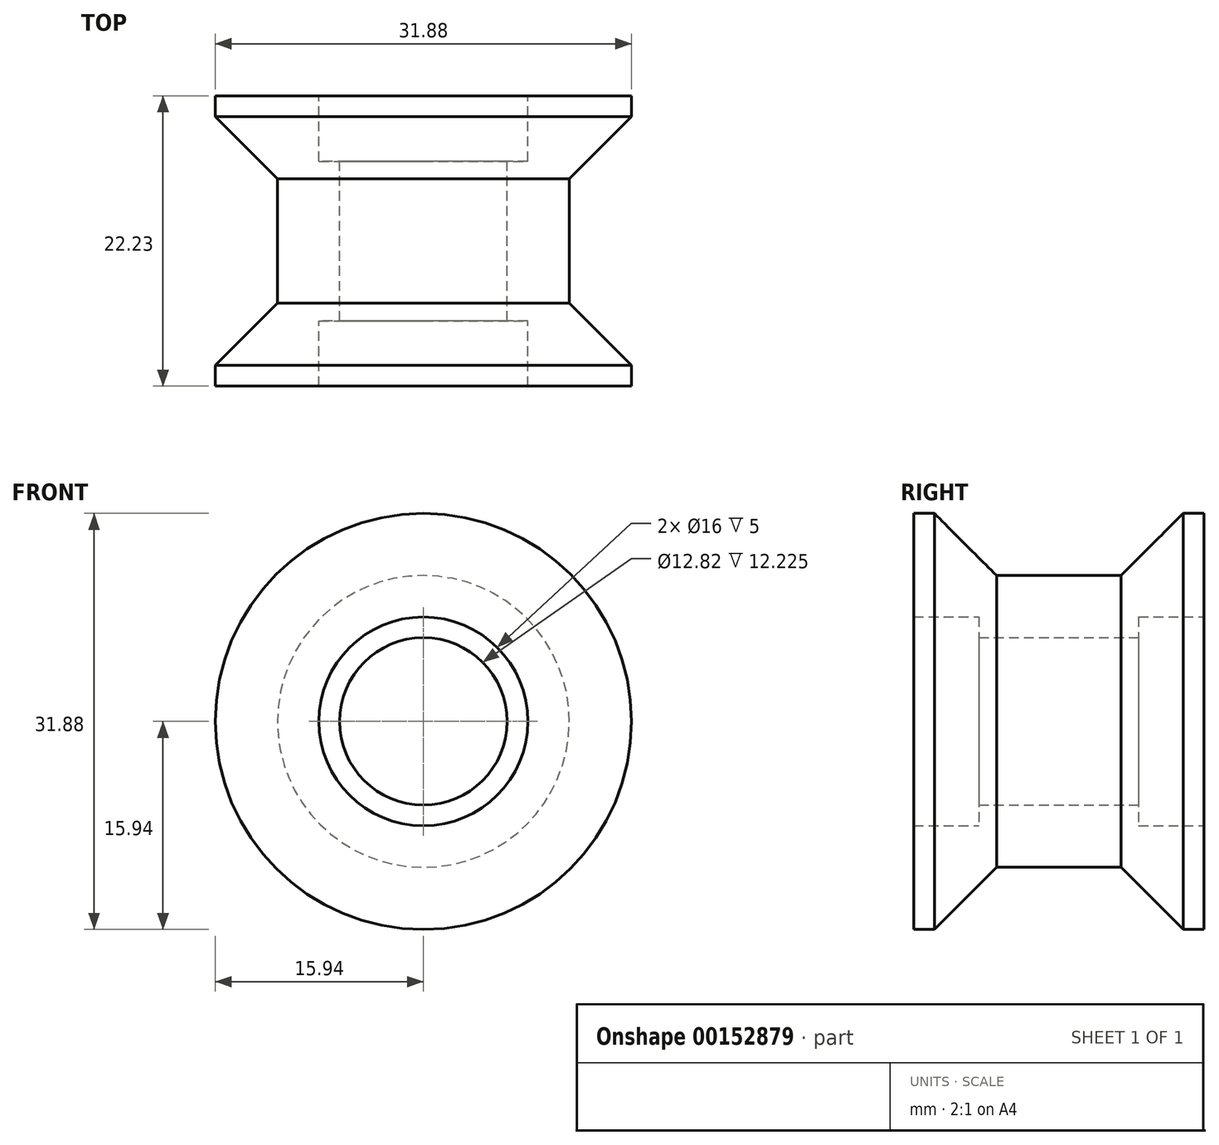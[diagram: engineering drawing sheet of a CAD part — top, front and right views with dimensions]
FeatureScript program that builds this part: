
annotation { "Feature Type Name" : "Feature", "Feature Type Description" : "" }
export const myFeature = defineFeature(function(context is Context, id is Id, definition is map)
    precondition{}
    {
        {
            var Q0;
            Q0=qCreatedBy(makeId("Top.planeOp"),FACE);
            var sketch = newSketch(context, id + "F0", { "sketchPlane" : qUnion([Q0])});
            skLineSegment(sketch, "E0", {"start": v(-15.94, 0) * mm, "end": v(-15.94, 1.59) * mm});
            skLineSegment(sketch, "E1", {"start": v(-15.94, 1.59) * mm, "end": v(-11.18, 6.35) * mm});
            skLineSegment(sketch, "E2", {"start": v(-11.18, 6.35) * mm, "end": v(-11.18, 15.88) * mm});
            skLineSegment(sketch, "E3", {"start": v(-11.18, 15.88) * mm, "end": v(-15.94, 20.64) * mm});
            skLineSegment(sketch, "E4", {"start": v(-15.94, 20.64) * mm, "end": v(-15.94, 22.23) * mm});
            skLineSegment(sketch, "E5", {"start": v(-15.94, 22.23) * mm, "end": v(-8, 22.23) * mm});
            skLineSegment(sketch, "E6.bottom", {"start": v(0, 0) * mm, "end": v(-8, 0) * mm, "construction": true});
            skLineSegment(sketch, "E6.top", {"start": v(0, 22.23) * mm, "end": v(-8, 22.23) * mm, "construction": true});
            skLineSegment(sketch, "E6.left", {"start": v(0, 0) * mm, "end": v(0, 22.23) * mm, "construction": true});
            skLineSegment(sketch, "E7", {"start": v(-8, 0) * mm, "end": v(-15.94, 0) * mm});
            skLineSegment(sketch, "E8", {"start": v(-15.94, 1.59) * mm, "end": v(-15.94, 20.64) * mm, "construction": true});
            skLineSegment(sketch, "E9", {"start": v(-15.94, 11.11) * mm, "end": v(-11.18, 11.11) * mm, "construction": true});
            skLineSegment(sketch, "E10", {"start": v(-11.18, 11.11) * mm, "end": v(-8, 11.11) * mm, "construction": true});
            skLineSegment(sketch, "E11.bottom", {"start": v(-8, 17.23) * mm, "end": v(-6.41, 17.23) * mm});
            skLineSegment(sketch, "E11.top", {"start": v(-8, 5) * mm, "end": v(-6.41, 5) * mm});
            skLineSegment(sketch, "E11.left", {"start": v(-8, 17.23) * mm, "end": v(-8, 5) * mm, "construction": true});
            skLineSegment(sketch, "E11.right", {"start": v(-6.41, 17.23) * mm, "end": v(-6.41, 5) * mm});
            skLineSegment(sketch, "E12", {"start": v(-8, 0) * mm, "end": v(-8, 5) * mm});
            skLineSegment(sketch, "E13", {"start": v(-8, 22.23) * mm, "end": v(-8, 17.23) * mm});
            skSolve(sketch);
        }
        {
            var Q0;
            Q0=qCreatedBy(makeId("Front.planeOp"),FACE);
            var sketch = newSketch(context, id + "F1", { "sketchPlane" : qUnion([Q0])});
            skCircle(sketch, "E14", {"center": v(0, 0) * mm, "radius": 1.59 * mm});
            skSolve(sketch);
        }
        {
            var Q0;
            Q0=makeQuery(id+"F0.imprint","IMPRINT",FACE,{"disambiguationData":[TD([[makeQuery(id+"F0.imprint","IMPRINT",EDGE,{"derivedFrom":sQuery(id+"F0.wireOp",EDGE,"E0")}),-1.0]])]});
            var Q1;
            Q1=sQuery(id+"F1.wireOp",EDGE,"E14");
            revolve(context, id + "F2", {"entities" : qUnion([Q0]), "axis" : qUnion([Q1]), "revolveType" : RevolveType.FULL});
        }
    });
